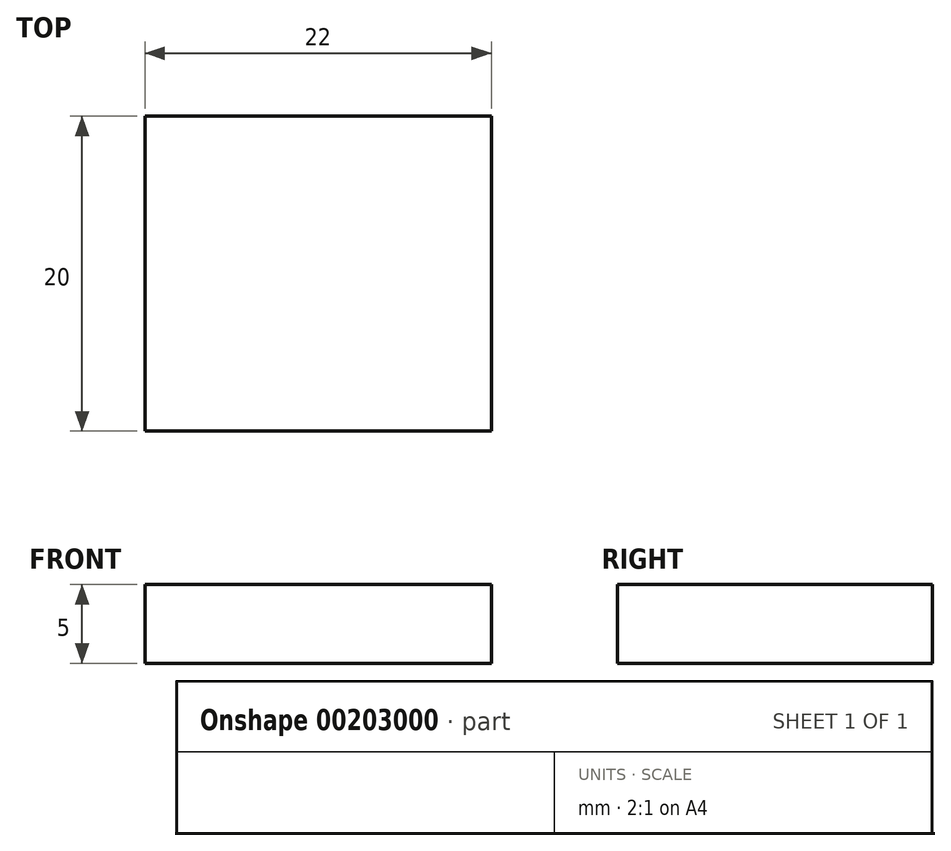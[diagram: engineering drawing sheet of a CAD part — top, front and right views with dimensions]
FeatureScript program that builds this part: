
annotation { "Feature Type Name" : "Feature", "Feature Type Description" : "" }
export const myFeature = defineFeature(function(context is Context, id is Id, definition is map)
    precondition{}
    {
        {
            var Q0;
            Q0=qCreatedBy(makeId("Top.planeOp"),FACE);
            var sketch = newSketch(context, id + "F0", { "sketchPlane" : qUnion([Q0])});
            skLineSegment(sketch, "E0.bottom", {"start": v(-11, -10) * mm, "end": v(11, -10) * mm});
            skLineSegment(sketch, "E0.top", {"start": v(-11, 10) * mm, "end": v(11, 10) * mm});
            skLineSegment(sketch, "E0.left", {"start": v(-11, -10) * mm, "end": v(-11, 10) * mm});
            skLineSegment(sketch, "E0.right", {"start": v(11, -10) * mm, "end": v(11, 10) * mm});
            skPoint(sketch, "E0.middle", {"position": v(0, 0) * mm});
            skSolve(sketch);
        }
        {
            var Q0;
            Q0 = qSketchRegion(id + "F0", true);
            extrude(context, id + "F1", {"entities" : qUnion([Q0]), "depth" : 5 * mm});
        }
    });
